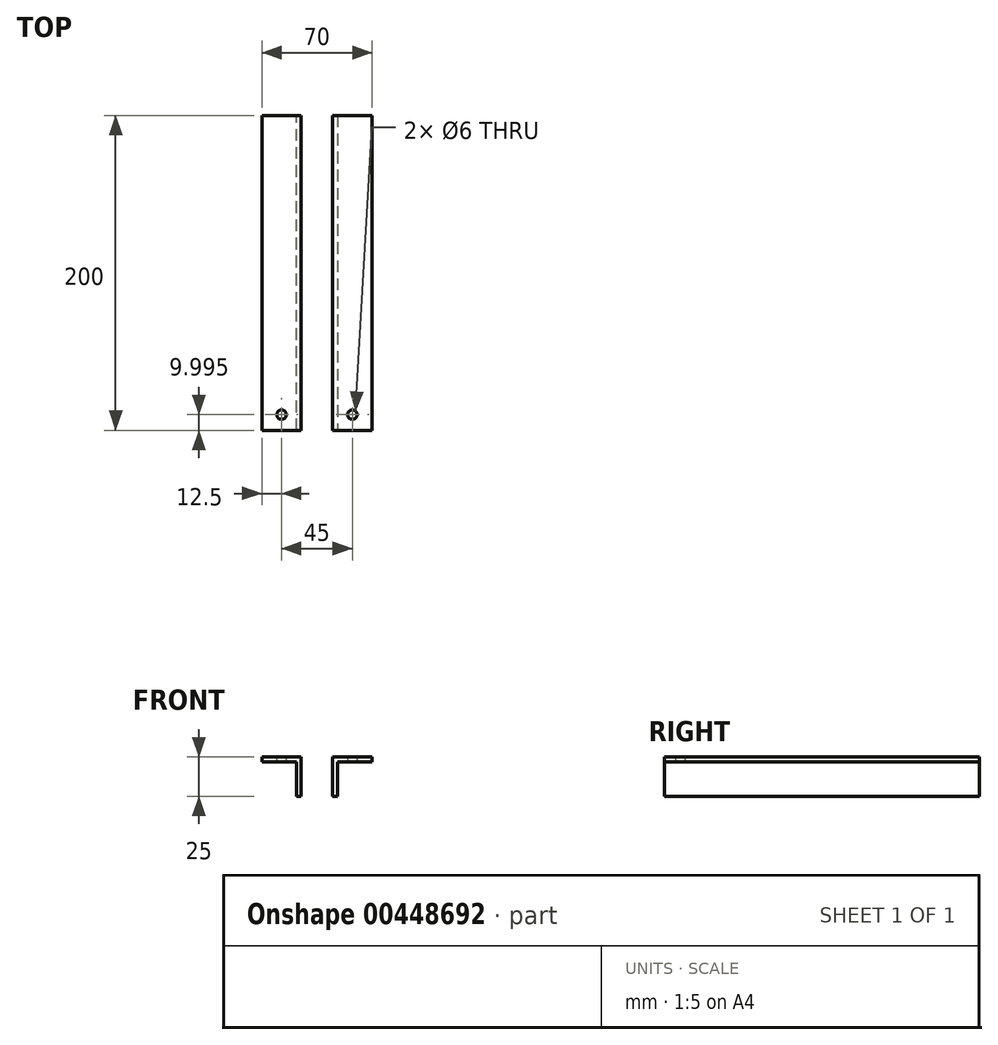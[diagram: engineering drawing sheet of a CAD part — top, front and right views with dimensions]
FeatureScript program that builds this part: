
annotation { "Feature Type Name" : "Feature", "Feature Type Description" : "" }
export const myFeature = defineFeature(function(context is Context, id is Id, definition is map)
    precondition{}
    {
        {
            var Q0;
            Q0=qCreatedBy(makeId("Top.planeOp"),FACE);
            var sketch = newSketch(context, id + "F0", { "sketchPlane" : qUnion([Q0])});
            skLineSegment(sketch, "E0.bottom", {"start": v(-45, 65.99) * mm, "end": v(-20, 65.99) * mm});
            skLineSegment(sketch, "E0.top", {"start": v(-45, -134.01) * mm, "end": v(-20, -134.01) * mm});
            skLineSegment(sketch, "E0.left", {"start": v(-45, 65.99) * mm, "end": v(-45, -134.01) * mm});
            skLineSegment(sketch, "E0.right", {"start": v(-20, 65.99) * mm, "end": v(-20, -134.01) * mm});
            skLineSegment(sketch, "E1.bottom", {"start": v(0, 65.99) * mm, "end": v(25, 65.99) * mm});
            skLineSegment(sketch, "E1.top", {"start": v(0, -134.01) * mm, "end": v(25, -134.01) * mm});
            skLineSegment(sketch, "E1.left", {"start": v(0, 65.99) * mm, "end": v(0, -134.01) * mm});
            skLineSegment(sketch, "E1.right", {"start": v(25, 65.99) * mm, "end": v(25, -134.01) * mm});
            skSolve(sketch);
        }
        {
            var Q0;
            Q0=makeQuery(id+"F0.imprint","IMPRINT",FACE,{"disambiguationData":[TD([[makeQuery(id+"F0.imprint","IMPRINT",EDGE,{"derivedFrom":sQuery(id+"F0.wireOp",EDGE,"E0.bottom")}),-1.0]])]});
            var Q1;
            Q1=makeQuery(id+"F0.imprint","IMPRINT",FACE,{"disambiguationData":[TD([[makeQuery(id+"F0.imprint","IMPRINT",EDGE,{"derivedFrom":sQuery(id+"F0.wireOp",EDGE,"E1.bottom")}),-1.0]])]});
            extrude(context, id + "F1", {"entities" : qUnion([Q0, Q1]), "oppositeDirection" : true, "depth" : 3 * mm});
        }
        {
            var Q0;
            Q0=makeQuery(id+"F1.opExtrude","CAP_FACE",FACE,{"disambiguationData":[OSD([sQuery(id+"F0.wireOp",EDGE,"E0.bottom"),sQuery(id+"F0.wireOp",EDGE,"E0.top"),sQuery(id+"F0.wireOp",EDGE,"E0.left"),sQuery(id+"F0.wireOp",EDGE,"E0.right")])],"isStart":false});
            var sketch = newSketch(context, id + "F2", { "sketchPlane" : qUnion([Q0])});
            skLineSegment(sketch, "E2", {"start": v(-20, 134.01) * mm, "end": v(-23, 134.01) * mm});
            skLineSegment(sketch, "E3", {"start": v(-23, 134.01) * mm, "end": v(-23, -65.99) * mm});
            skLineSegment(sketch, "E4", {"start": v(-23, -65.99) * mm, "end": v(-20, -65.99) * mm});
            skLineSegment(sketch, "E5", {"start": v(-20, -65.99) * mm, "end": v(-20, 134.01) * mm});
            skLineSegment(sketch, "E6", {"start": v(0, 134.01) * mm, "end": v(0, -65.99) * mm});
            skLineSegment(sketch, "E7", {"start": v(0, -65.99) * mm, "end": v(3, -65.99) * mm});
            skLineSegment(sketch, "E8", {"start": v(3, -65.99) * mm, "end": v(3, 134.01) * mm});
            skLineSegment(sketch, "E9", {"start": v(3, 134.01) * mm, "end": v(0, 134.01) * mm});
            skSolve(sketch);
        }
        {
            var Q0;
            Q0=makeQuery(id+"F2.imprint","IMPRINT",FACE,{"disambiguationData":[TD([[makeQuery(id+"F2.imprint","IMPRINT",EDGE,{"derivedFrom":sQuery(id+"F2.wireOp",EDGE,"E2")}),-1.0]])]});
            var Q1;
            Q1=makeQuery(id+"F2.imprint","IMPRINT",FACE,{"disambiguationData":[TD([[makeQuery(id+"F2.imprint","IMPRINT",EDGE,{"derivedFrom":sQuery(id+"F2.wireOp",EDGE,"E6")}),1.0]])]});
            extrude(context, id + "F3", {"entities" : qUnion([Q0, Q1]), "operationType" : NewBodyOperationType.ADD, "depth" : 22 * mm});
        }
        {
            var Q0;
            Q0=makeQuery(id+"F1.opExtrude","CAP_FACE",FACE,{"disambiguationData":[OSD([sQuery(id+"F0.wireOp",EDGE,"E0.bottom"),sQuery(id+"F0.wireOp",EDGE,"E0.top"),sQuery(id+"F0.wireOp",EDGE,"E0.left"),sQuery(id+"F0.wireOp",EDGE,"E0.right")])],"isStart":false});
            var sketch = newSketch(context, id + "F4", { "sketchPlane" : qUnion([Q0])});
            skLineSegment(sketch, "E10", {"start": v(-45, 134.01) * mm, "end": v(-32.5, 134.01) * mm});
            skLineSegment(sketch, "E11", {"start": v(-32.5, 134.01) * mm, "end": v(-32.5, 124.01) * mm});
            skLineSegment(sketch, "E12", {"start": v(-32.5, 124.01) * mm, "end": v(12.5, 124.01) * mm});
            skCircle(sketch, "E13", {"center": v(-32.5, 124.01) * mm, "radius": 3 * mm});
            skCircle(sketch, "E14", {"center": v(12.5, 124.01) * mm, "radius": 3 * mm});
            skSolve(sketch);
        }
        {
            var Q0;
            Q0=sQuery(id+"F4.wireOp",VERTEX,"E13.center");
            var Q1;
            Q1=sQuery(id+"F4.wireOp",VERTEX,"E12.end");
            var Q2;
            Q2=makeQuery(id+"F1.opExtrude","SWEPT_BODY",BODY,{"disambiguationData":[OSD([sQuery(id+"F0.wireOp",EDGE,"E0.bottom"),sQuery(id+"F0.wireOp",EDGE,"E0.top"),sQuery(id+"F0.wireOp",EDGE,"E0.left"),sQuery(id+"F0.wireOp",EDGE,"E0.right")])]});
            var Q3;
            Q3=makeQuery(id+"F1.opExtrude","SWEPT_BODY",BODY,{"disambiguationData":[OSD([sQuery(id+"F0.wireOp",EDGE,"E1.bottom"),sQuery(id+"F0.wireOp",EDGE,"E1.top"),sQuery(id+"F0.wireOp",EDGE,"E1.left"),sQuery(id+"F0.wireOp",EDGE,"E1.right")])]});
            hole(context, id + "F5", {"style" : HoleStyle.SIMPLE, "endStyle" : HoleEndStyle.BLIND, "holeDiameter" : 6 * mm, "holeDepth" : 7 * mm, "isTappedThrough" : true, "tappedDepth" : 12 * mm, "tapClearance" : 3, "locations" : qUnion([Q0, Q1]), "scope" : qUnion([Q2, Q3])});
        }
        {
            var Q0;
            Q0=makeQuery(id+"F1.opExtrude","SWEPT_BODY",BODY,{"disambiguationData":[OSD([sQuery(id+"F0.wireOp",EDGE,"E0.bottom"),sQuery(id+"F0.wireOp",EDGE,"E0.top"),sQuery(id+"F0.wireOp",EDGE,"E0.left"),sQuery(id+"F0.wireOp",EDGE,"E0.right")])]});
            transform(context, id + "F6", {"entities" : qUnion([Q0]), "transformType" : TransformType.TRANSLATION_3D, "dx" : 0 * mm, "dy" : 0 * mm, "dz" : 0 * mm, "makeCopy" : true});
        }
        {
            var Q0;
            Q0=makeQuery(id+"F6.opPattern","COPY",BODY,{"derivedFrom":makeQuery(id+"F1.opExtrude","SWEPT_BODY",BODY,{"disambiguationData":[OSD([sQuery(id+"F0.wireOp",EDGE,"E0.bottom"),sQuery(id+"F0.wireOp",EDGE,"E0.top"),sQuery(id+"F0.wireOp",EDGE,"E0.left"),sQuery(id+"F0.wireOp",EDGE,"E0.right")])]}),"instanceName":"1"});
            deleteBodies(context, id + "F7", {"entities" : qUnion([Q0])});
        }
    });
